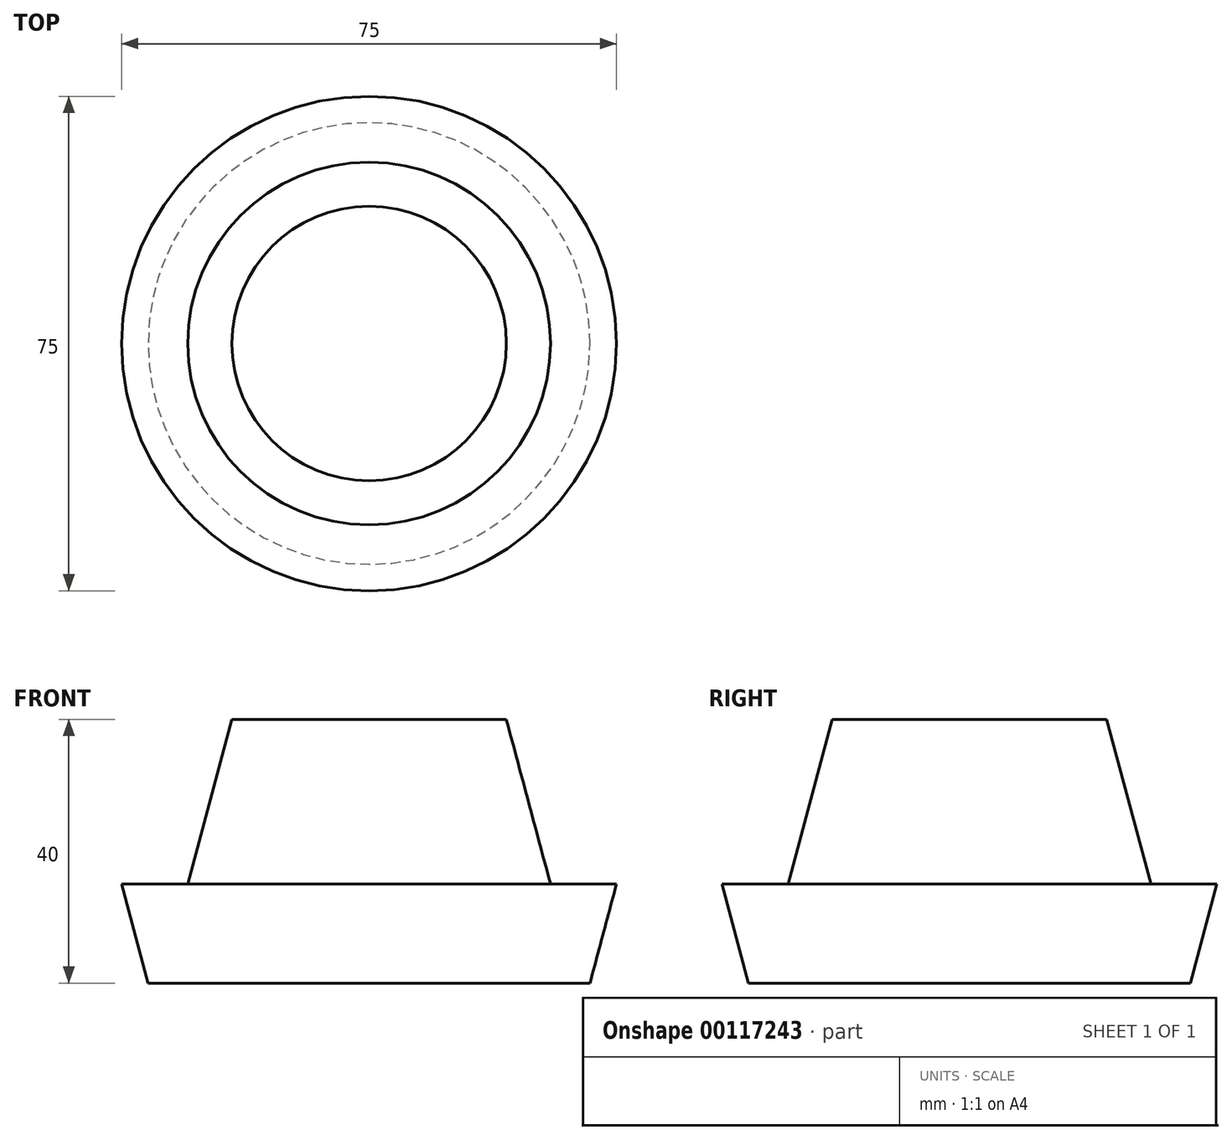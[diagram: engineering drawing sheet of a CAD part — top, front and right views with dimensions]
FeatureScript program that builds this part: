
annotation { "Feature Type Name" : "Feature", "Feature Type Description" : "" }
export const myFeature = defineFeature(function(context is Context, id is Id, definition is map)
    precondition{}
    {
        {
            var Q0;
            Q0=qCreatedBy(makeId("Top.planeOp"),FACE);
            var sketch = newSketch(context, id + "F0", { "sketchPlane" : qUnion([Q0])});
            skCircle(sketch, "E0", {"center": v(0, 0) * mm, "radius": 37.5 * mm});
            skCircle(sketch, "E1", {"center": v(0, 0) * mm, "radius": 27.5 * mm});
            skSolve(sketch);
        }
        {
            var Q0;
            Q0=makeQuery(id+"F0.imprint","IMPRINT",FACE,{"disambiguationData":[TD([[makeQuery(id+"F0.imprint","IMPRINT",EDGE,{"derivedFrom":sQuery(id+"F0.wireOp",EDGE,"E1")}),1.0]])]});
            extrude(context, id + "F1", {"entities" : qUnion([Q0]), "depth" : 25 * mm, "hasDraft" : true, "draftAngle" : 15 * degree, "draftPullDirection" : true});
        }
        {
            var Q0;
            Q0=makeQuery(id+"F0.imprint","IMPRINT",FACE,{"disambiguationData":[TD([[makeQuery(id+"F0.imprint","IMPRINT",EDGE,{"derivedFrom":sQuery(id+"F0.wireOp",EDGE,"E1")}),1.0]])]});
            var Q1;
            Q1=makeQuery(id+"F0.imprint","IMPRINT",FACE,{"disambiguationData":[TD([[makeQuery(id+"F0.imprint","IMPRINT",EDGE,{"derivedFrom":sQuery(id+"F0.wireOp",EDGE,"E0")}),1.0]])]});
            extrude(context, id + "F2", {"entities" : qUnion([Q0, Q1]), "operationType" : NewBodyOperationType.ADD, "oppositeDirection" : true, "depth" : 15 * mm, "hasDraft" : true, "draftAngle" : 15 * degree, "draftPullDirection" : true});
        }
    });
